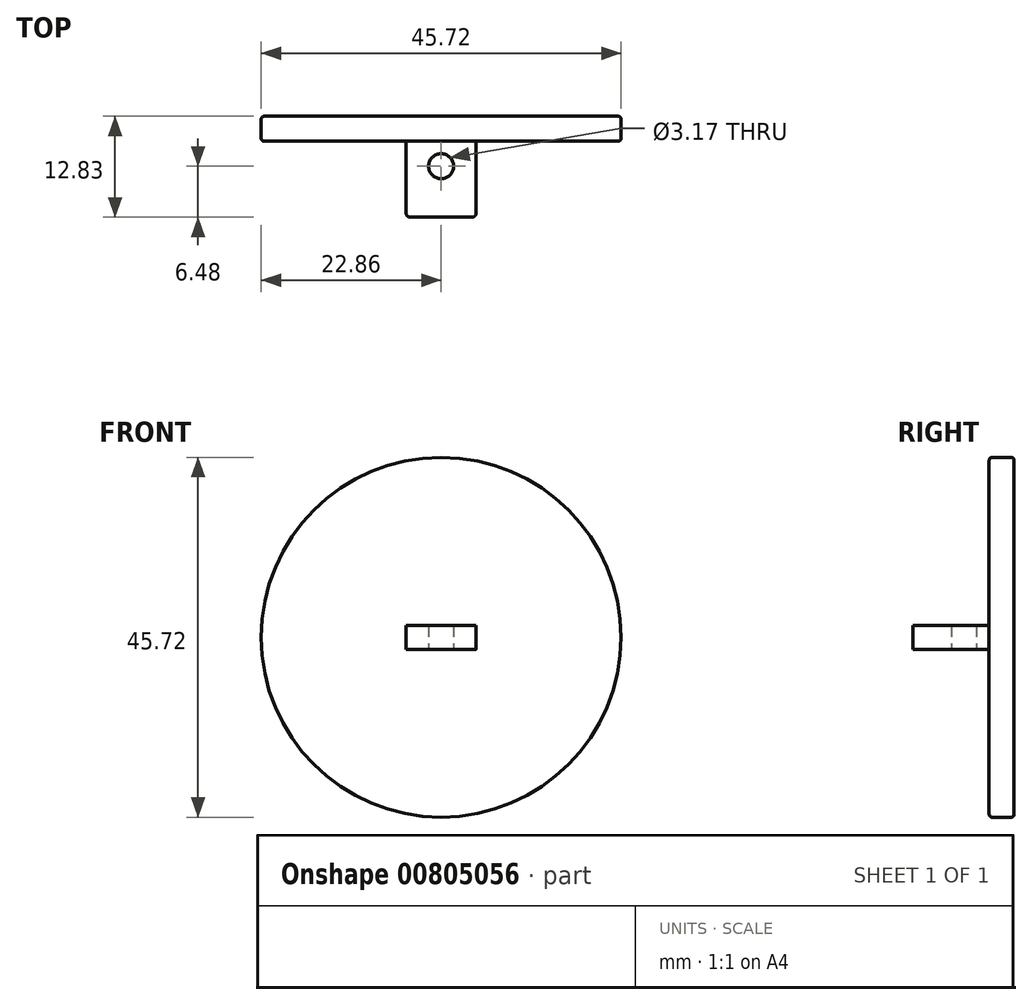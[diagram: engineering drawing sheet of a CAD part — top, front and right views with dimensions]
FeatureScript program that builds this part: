
annotation { "Feature Type Name" : "Feature", "Feature Type Description" : "" }
export const myFeature = defineFeature(function(context is Context, id is Id, definition is map)
    precondition{}
    {
        {
            var Q0;
            Q0=qCreatedBy(makeId("Front.planeOp"),FACE);
            var sketch = newSketch(context, id + "F0", { "sketchPlane" : qUnion([Q0])});
            skCircle(sketch, "E0", {"center": v(0, 0) * mm, "radius": 22.86 * mm});
            skSolve(sketch);
        }
        {
            var Q0;
            Q0=makeQuery(id+"F0.imprint","IMPRINT",FACE,{"disambiguationData":[TD([[makeQuery(id+"F0.imprint","IMPRINT",EDGE,{"derivedFrom":sQuery(id+"F0.wireOp",EDGE,"E0")}),1.0]])]});
            extrude(context, id + "F1", {"entities" : qUnion([Q0]), "depth" : 3.17 * mm, "offsetDistance" : 25.4 * mm});
        }
        {
            var Q0;
            Q0=makeQuery(id+"F1.opExtrude","CAP_FACE",FACE,{"disambiguationData":[OSD([sQuery(id+"F0.wireOp",EDGE,"E0")])],"isStart":false});
            var sketch = newSketch(context, id + "F2", { "sketchPlane" : qUnion([Q0])});
            skLineSegment(sketch, "E1.bottom", {"start": v(-4.45, 1.52) * mm, "end": v(4.45, 1.52) * mm});
            skLineSegment(sketch, "E1.top", {"start": v(-4.44, -1.52) * mm, "end": v(4.44, -1.52) * mm});
            skLineSegment(sketch, "E1.left", {"start": v(-4.45, 1.52) * mm, "end": v(-4.45, -1.52) * mm});
            skLineSegment(sketch, "E1.right", {"start": v(4.45, 1.52) * mm, "end": v(4.45, -1.52) * mm});
            skPoint(sketch, "E1.middle", {"position": v(0, 0) * mm});
            skSolve(sketch);
        }
        {
            var Q0;
            Q0=makeQuery(id+"F2.imprint","IMPRINT",FACE,{"disambiguationData":[TD([[makeQuery(id+"F2.imprint","IMPRINT",EDGE,{"derivedFrom":sQuery(id+"F2.wireOp",EDGE,"E1.bottom")}),-1.0]])]});
            extrude(context, id + "F3", {"entities" : qUnion([Q0]), "operationType" : NewBodyOperationType.ADD, "depth" : 9.65 * mm, "offsetDistance" : 25.4 * mm});
        }
        {
            var Q0;
            Q0=makeQuery(id+"F3.opExtrude","SWEPT_FACE",FACE,{"disambiguationData":[OSD([sQuery(id+"F2.wireOp",EDGE,"E1.top")])]});
            var sketch = newSketch(context, id + "F4", { "sketchPlane" : qUnion([Q0])});
            skCircle(sketch, "E2", {"center": v(0, 6.35) * mm, "radius": 1.59 * mm});
            skSolve(sketch);
        }
        {
            var Q0;
            Q0=makeQuery(id+"F4.imprint","IMPRINT",FACE,{"disambiguationData":[TD([[makeQuery(id+"F4.imprint","IMPRINT",EDGE,{"derivedFrom":sQuery(id+"F4.wireOp",EDGE,"E2")}),1.0]])]});
            extrude(context, id + "F5", {"entities" : qUnion([Q0]), "operationType" : NewBodyOperationType.REMOVE, "endBound" : BoundingType.THROUGH_ALL, "oppositeDirection" : true, "depth" : 25.4 * mm, "offsetDistance" : 25.4 * mm});
        }
        {
            var Q0;
            Q0=makeQuery(id+"F3.opExtrude","CAP_EDGE",EDGE,{"disambiguationData":[OSD([sQuery(id+"F2.wireOp",EDGE,"E1.left")])],"isStart":false});
            var Q1;
            Q1=makeQuery(id+"F3.opExtrude","CAP_EDGE",EDGE,{"disambiguationData":[OSD([sQuery(id+"F2.wireOp",EDGE,"E1.right")])],"isStart":false});
            var Q2;
            Q2=makeQuery(id+"F3.opExtrude","CAP_EDGE",EDGE,{"disambiguationData":[OSD([sQuery(id+"F2.wireOp",EDGE,"E1.top")])],"isStart":true});
            var Q3;
            Q3=makeQuery(id+"F3.opExtrude","CAP_EDGE",EDGE,{"disambiguationData":[OSD([sQuery(id+"F2.wireOp",EDGE,"E1.left")])],"isStart":true});
            var Q4;
            Q4=makeQuery(id+"F3.opExtrude","CAP_EDGE",EDGE,{"disambiguationData":[OSD([sQuery(id+"F2.wireOp",EDGE,"E1.right")])],"isStart":true});
            var Q5;
            Q5=makeQuery(id+"F3.opExtrude","CAP_EDGE",EDGE,{"disambiguationData":[OSD([sQuery(id+"F2.wireOp",EDGE,"E1.bottom")])],"isStart":true});
            fillet(context, id + "F6", {"entities" : qUnion([Q0, Q1, Q2, Q3, Q4, Q5]), "radius" : 0.5 * mm, "tangentPropagation" : true, "allowEdgeOverflow" : false});
        }
        {
            var Q0;
            Q0=makeQuery(id+"F1.opExtrude","CAP_EDGE",EDGE,{"disambiguationData":[OSD([sQuery(id+"F0.wireOp",EDGE,"E0")])],"isStart":false});
            var Q1;
            Q1=makeQuery(id+"F1.opExtrude","CAP_EDGE",EDGE,{"disambiguationData":[OSD([sQuery(id+"F0.wireOp",EDGE,"E0")])],"isStart":true});
            fillet(context, id + "F7", {"entities" : qUnion([Q0, Q1]), "radius" : 0.38 * mm, "tangentPropagation" : true, "allowEdgeOverflow" : false});
        }
    });
